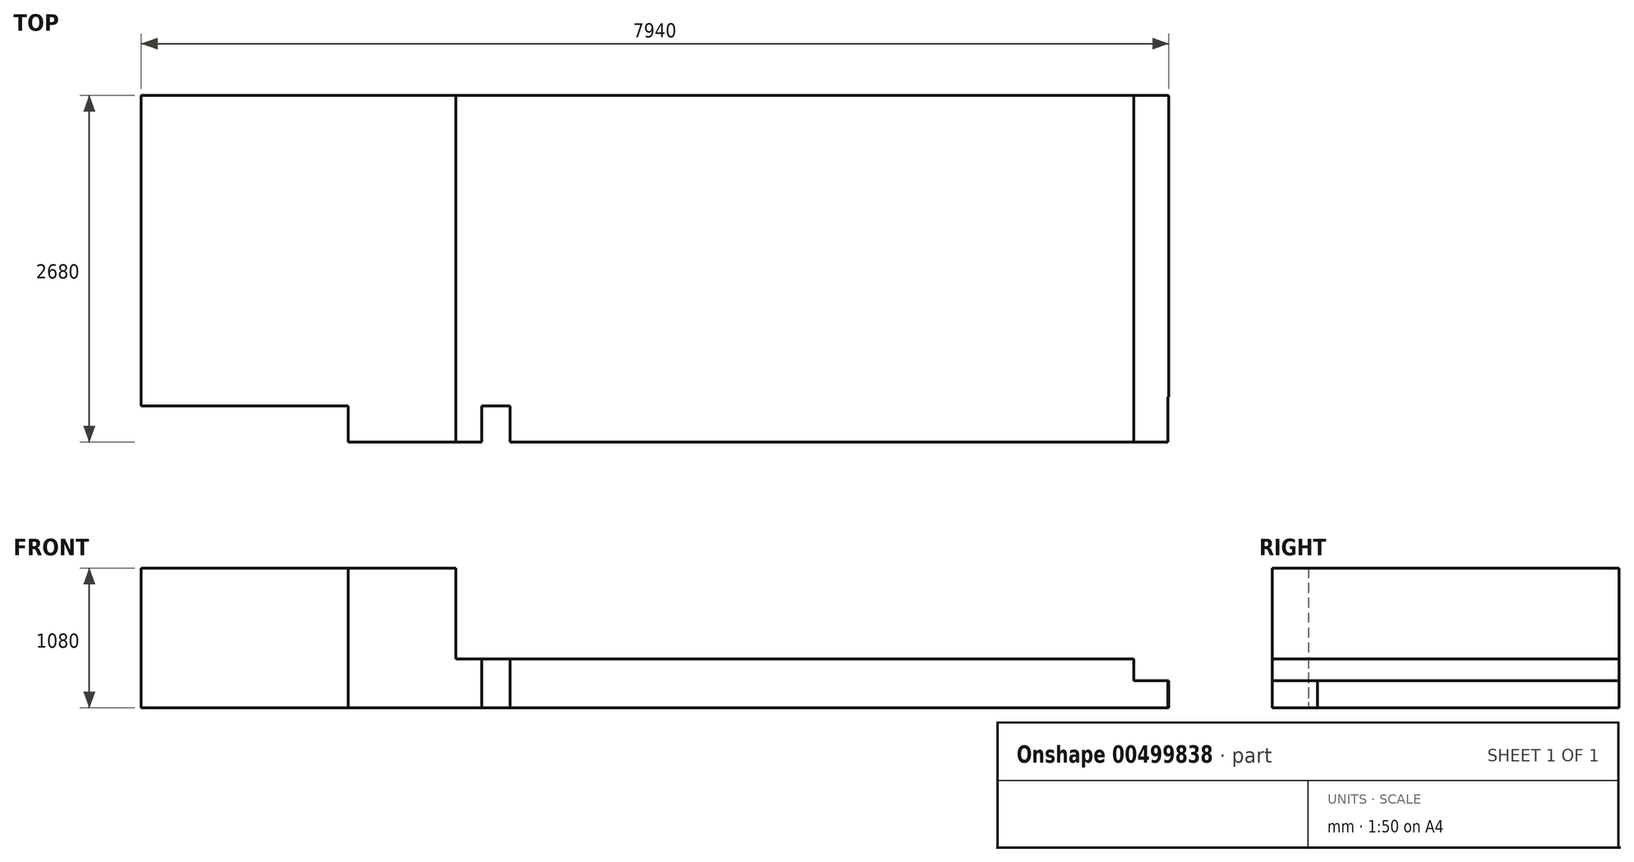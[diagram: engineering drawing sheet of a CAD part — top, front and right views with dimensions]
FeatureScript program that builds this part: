
annotation { "Feature Type Name" : "Feature", "Feature Type Description" : "" }
export const myFeature = defineFeature(function(context is Context, id is Id, definition is map)
    precondition{}
    {
        {
            var Q0;
            Q0=qCreatedBy(makeId("Top.planeOp"),FACE);
            var sketch = newSketch(context, id + "F0", { "sketchPlane" : qUnion([Q0])});
            skLineSegment(sketch, "E0", {"start": v(-9750, 0) * mm, "end": v(-9750, -2400) * mm});
            skLineSegment(sketch, "E1", {"start": v(-9750, -2400) * mm, "end": v(-9750, -2950) * mm});
            skLineSegment(sketch, "E2", {"start": v(-9750, -2950) * mm, "end": v(-9750, -6950) * mm});
            skLineSegment(sketch, "E3", {"start": v(-9750, -6950) * mm, "end": v(-2200, -6950) * mm});
            skLineSegment(sketch, "E4", {"start": v(-2200, -6950) * mm, "end": v(-2200, -2950) * mm});
            skLineSegment(sketch, "E5", {"start": v(-2200, -2950) * mm, "end": v(-7120, -2950) * mm});
            skLineSegment(sketch, "E6", {"start": v(-7120, -2950) * mm, "end": v(-7120, -2400) * mm});
            skLineSegment(sketch, "E7", {"start": v(-7120, -2400) * mm, "end": v(-6900, -2400) * mm});
            skLineSegment(sketch, "E8", {"start": v(-6900, -2400) * mm, "end": v(-6900, -2680) * mm});
            skLineSegment(sketch, "E9", {"start": v(-6900, -2680) * mm, "end": v(-1815, -2680) * mm});
            skLineSegment(sketch, "E10", {"start": v(-1815, -2680) * mm, "end": v(-1815, -2330) * mm});
            skLineSegment(sketch, "E11", {"start": v(-1815, -2330) * mm, "end": v(0, -2330) * mm});
            skLineSegment(sketch, "E12", {"start": v(0, -2330) * mm, "end": v(0, -1090) * mm});
            skLineSegment(sketch, "E13", {"start": v(0, -1090) * mm, "end": v(0, -240) * mm});
            skLineSegment(sketch, "E14", {"start": v(0, -240) * mm, "end": v(0, 0) * mm});
            skLineSegment(sketch, "E15", {"start": v(0, 0) * mm, "end": v(-9750, 0) * mm});
            skLineSegment(sketch, "E16", {"start": v(-9750, -2400) * mm, "end": v(-8150, -2400) * mm});
            skLineSegment(sketch, "E17", {"start": v(-8150, -2400) * mm, "end": v(-8150, -2950) * mm});
            skLineSegment(sketch, "E18", {"start": v(-8150, -2950) * mm, "end": v(-9750, -2950) * mm});
            skLineSegment(sketch, "E19", {"start": v(-6420, -2950) * mm, "end": v(-6420, -4010) * mm});
            skLineSegment(sketch, "E20", {"start": v(-6420, -4010) * mm, "end": v(-5360, -4010) * mm});
            skLineSegment(sketch, "E21", {"start": v(-5360, -4010) * mm, "end": v(-5360, -2950) * mm});
            skLineSegment(sketch, "E22", {"start": v(0, 0) * mm, "end": v(145, 0) * mm});
            skLineSegment(sketch, "E23", {"start": v(145, 0) * mm, "end": v(145, -5370) * mm});
            skLineSegment(sketch, "E24", {"start": v(145, -5370) * mm, "end": v(0, -5370) * mm});
            skLineSegment(sketch, "E25", {"start": v(0, -5370) * mm, "end": v(0, -2330) * mm});
            skLineSegment(sketch, "E26", {"start": v(0, -2475) * mm, "end": v(-1670, -2475) * mm});
            skLineSegment(sketch, "E27", {"start": v(-1670, -2475) * mm, "end": v(-1670, -2950) * mm});
            skLineSegment(sketch, "E28", {"start": v(-1670, -2950) * mm, "end": v(-1900, -2950) * mm});
            skLineSegment(sketch, "E29", {"start": v(-1900, -2950) * mm, "end": v(-1900, -7250) * mm});
            skLineSegment(sketch, "E30", {"start": v(-1900, -7250) * mm, "end": v(-2200, -6950) * mm});
            skLineSegment(sketch, "E31", {"start": v(-1900, -7250) * mm, "end": v(-10050, -7250) * mm});
            skLineSegment(sketch, "E32", {"start": v(-10050, -7250) * mm, "end": v(-9750, -6950) * mm});
            skLineSegment(sketch, "E33", {"start": v(-10050, -7250) * mm, "end": v(-10050, 300) * mm});
            skLineSegment(sketch, "E34", {"start": v(-10050, 300) * mm, "end": v(-9750, 0) * mm});
            skLineSegment(sketch, "E35", {"start": v(-10050, 300) * mm, "end": v(145, 300) * mm});
            skLineSegment(sketch, "E36", {"start": v(145, 300) * mm, "end": v(145, 0) * mm});
            skLineSegment(sketch, "E37", {"start": v(-8150, -2400) * mm, "end": v(-7120, -2400) * mm});
            skSolve(sketch);
        }
        {
            var Q0;
            Q0=qCreatedBy(makeId("Front.planeOp"),FACE);
            var sketch = newSketch(context, id + "F1", { "sketchPlane" : qUnion([Q0])});
            skLineSegment(sketch, "E38", {"start": v(-1810, 0) * mm, "end": v(-1810, 210) * mm});
            skLineSegment(sketch, "E39", {"start": v(-1810, 210) * mm, "end": v(-2080, 210) * mm});
            skLineSegment(sketch, "E40", {"start": v(-2080, 210) * mm, "end": v(-2080, 380) * mm});
            skLineSegment(sketch, "E41", {"start": v(-2080, 380) * mm, "end": v(-7320, 380) * mm});
            skLineSegment(sketch, "E42", {"start": v(-7320, 380) * mm, "end": v(-7320, 1080) * mm});
            skLineSegment(sketch, "E43", {"start": v(-7320, 1080) * mm, "end": v(-9750, 1080) * mm});
            skLineSegment(sketch, "E44", {"start": v(-9750, 1080) * mm, "end": v(-9750, 0) * mm});
            skLineSegment(sketch, "E45", {"start": v(-9750, 0) * mm, "end": v(-1810, 0) * mm});
            skCircle(sketch, "E46", {"center": v(-4700, 930) * mm, "radius": 125 * mm});
            skSolve(sketch);
        }
        {
            var Q0;
            Q0=makeQuery(id+"F1.imprint","IMPRINT",FACE,{"disambiguationData":[TD([[makeQuery(id+"F1.imprint","IMPRINT",EDGE,{"derivedFrom":sQuery(id+"F1.wireOp",EDGE,"E38")}),1.0]])]});
            var Q1;
            Q1=sQuery(id+"F0.wireOp",VERTEX,"E10.start");
            extrude(context, id + "F2", {"entities" : qUnion([Q0]), "endBound" : BoundingType.UP_TO_VERTEX, "endBoundEntityVertex" : qUnion([Q1]), "depth" : 25 * mm});
        }
        {
            var Q0;
            Q0=makeQuery(id+"F0.imprint","IMPRINT",FACE,{"disambiguationData":[TD([[makeQuery(id+"F0.imprint","IMPRINT",EDGE,{"derivedFrom":sQuery(id+"F0.wireOp",EDGE,"E1")}),1.0]])]});
            var Q1;
            Q1=makeQuery(id+"F2.opExtrude","SWEPT_FACE",FACE,{"disambiguationData":[OSD([sQuery(id+"F1.wireOp",EDGE,"E43")])]});
            extrude(context, id + "F3", {"entities" : qUnion([Q0]), "operationType" : NewBodyOperationType.REMOVE, "endBound" : BoundingType.UP_TO_SURFACE, "endBoundEntityFace" : qUnion([Q1]), "depth" : 25 * mm});
        }
        {
            var Q0;
            {var subQ2=sQuery(id+"F0.wireOp",EDGE,"E4");Q0=makeQuery(id+"F0.imprint","IMPRINT",FACE,{"disambiguationData":[TD([[makeQuery(id+"F0.imprint","IMPRINT",EDGE,{"derivedFrom":subQ2}),-1.0]])]});}
            var Q1;
            Q1=makeQuery(id+"F2.opExtrude","SWEPT_FACE",FACE,{"disambiguationData":[OSD([sQuery(id+"F1.wireOp",EDGE,"E41")])]});
            extrude(context, id + "F4", {"entities" : qUnion([Q0]), "operationType" : NewBodyOperationType.REMOVE, "endBound" : BoundingType.UP_TO_SURFACE, "endBoundEntityFace" : qUnion([Q1]), "depth" : 25 * mm});
        }
    });
